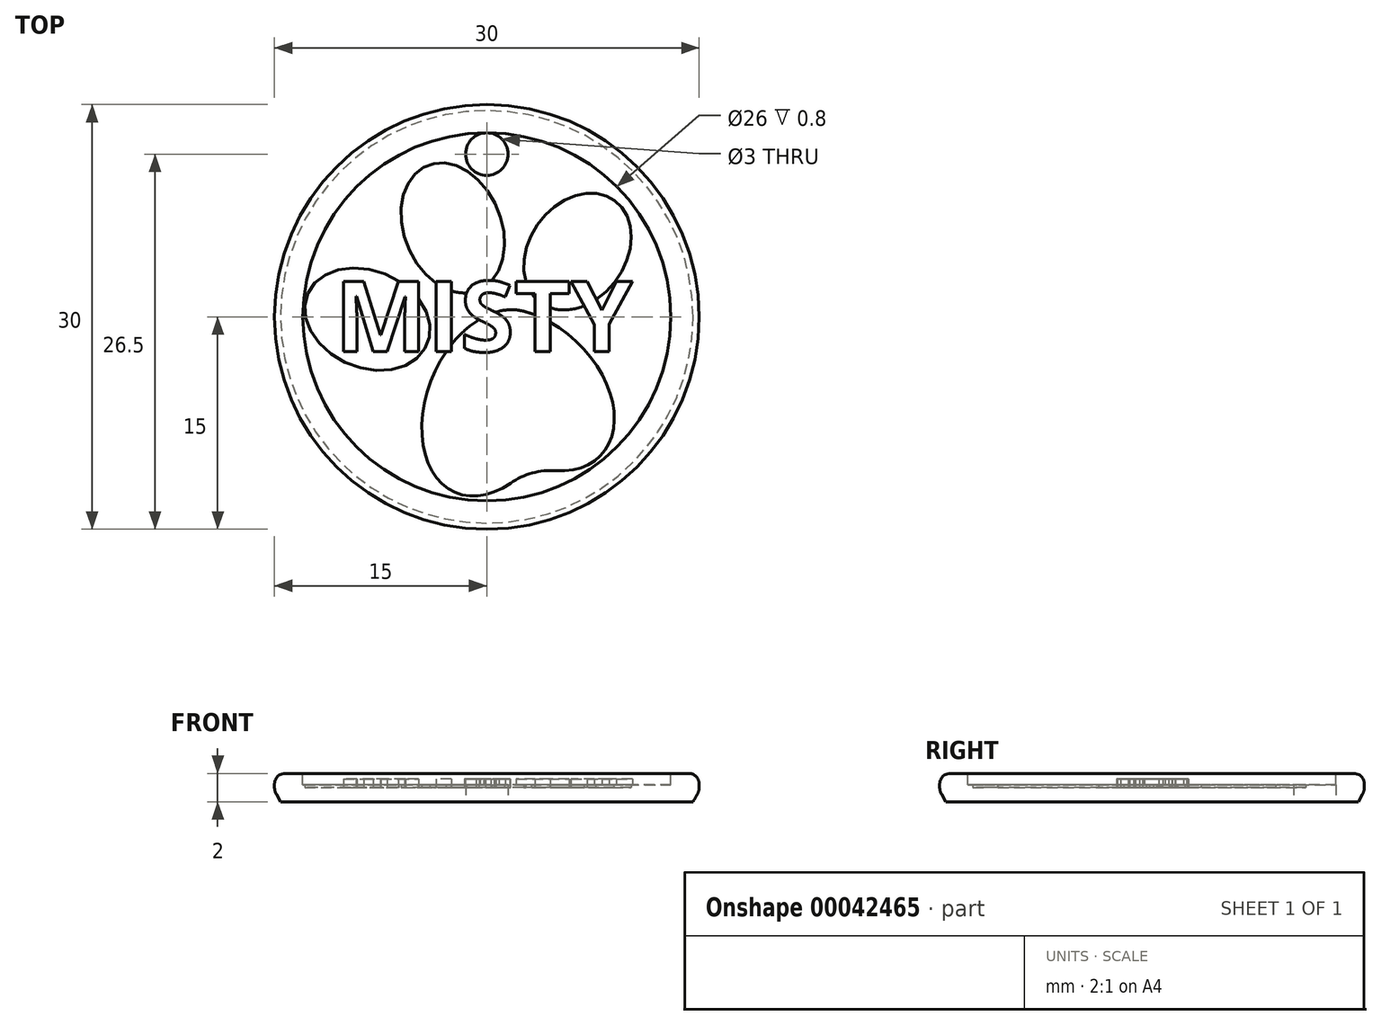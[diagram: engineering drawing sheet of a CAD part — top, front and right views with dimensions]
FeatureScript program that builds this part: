
annotation { "Feature Type Name" : "Feature", "Feature Type Description" : "" }
export const myFeature = defineFeature(function(context is Context, id is Id, definition is map)
    precondition{}
    {
        {
            var Q0;
            Q0=qCreatedBy(makeId("Top.planeOp"),FACE);
            var sketch = newSketch(context, id + "F0", { "sketchPlane" : qUnion([Q0])});
            skCircle(sketch, "E0", {"center": v(0, 0) * mm, "radius": 15 * mm});
            skSolve(sketch);
        }
        {
            var Q0;
            Q0 = qSketchRegion(id + "F0", true);
            extrude(context, id + "F1", {"entities" : qUnion([Q0]), "depth" : 2 * mm});
        }
        {
            var Q0;
            Q0=makeQuery(id+"F1.opExtrude","CAP_FACE",FACE,{"disambiguationData":[OSD([sQuery(id+"F0.wireOp",EDGE,"E0")])],"isStart":false});
            var sketch = newSketch(context, id + "F2", { "sketchPlane" : qUnion([Q0])});
            skCircle(sketch, "E1", {"center": v(0, 0) * mm, "radius": 13 * mm});
            skSolve(sketch);
        }
        {
            var Q0;
            Q0 = qSketchRegion(id + "F2", true);
            extrude(context, id + "F3", {"entities" : qUnion([Q0]), "operationType" : NewBodyOperationType.REMOVE, "oppositeDirection" : true, "depth" : 0.8 * mm});
        }
        {
            var Q0;
            Q0=makeQuery(id+"F3.boolean.opBoolean","COPY",FACE,{"derivedFrom":makeQuery(id+"F3.opExtrude","CAP_FACE",FACE,{"disambiguationData":[OSD([sQuery(id+"F2.wireOp",EDGE,"E1")])],"isStart":false})});
            var sketch = newSketch(context, id + "F4", { "sketchPlane" : qUnion([Q0])});
            skEllipse(sketch, "E2", {"center": v(-8.44, -0.16) * mm, "majorRadius": 4.58 * mm, "minorRadius": 3.42 * mm, "majorAxis": v(0.92, -0.39)});
            skEllipse(sketch, "E3", {"center": v(-2.4, 6.28) * mm, "majorRadius": 4.76 * mm, "minorRadius": 3.44 * mm, "majorAxis": v(0.38, -0.93)});
            skEllipse(sketch, "E4", {"center": v(6.4, 4.62) * mm, "majorRadius": 4.46 * mm, "minorRadius": 3.4 * mm, "majorAxis": v(0.58, 0.81)});
            skEllipticalArc(sketch, "E5", {});
            skEllipticalArc(sketch, "E6", {});
            skPoint(sketch, "E7.visualSharp", {"position": v(2.62, 0.4) * mm});
            skArc(sketch, "E7.filletArc", {"start": v(4.87, -10.86) * mm, "mid": v(3.2, -11.03) * mm, "end": v(1.68, -11.75) * mm});
            const initialGuessF4  = {"E5": [0.00039821620125618366, -0.006079853733279628, 0.3754317400528692, 0.9268500464265377, 0.006854673766816253, 0.004617638328241886, 0.08123967665926242, 3.942349918397179], "E6": [0.0031306940243142093, -0.005130720116552976, 0.7281276660444532, -0.6854415379452705, 0.006774684959826952, 0.004649626096762248, 5.58687193887531, 2.2321898580311177]};
            skSetInitialGuess(sketch, initialGuessF4);
            skSolve(sketch);
        }
        {
            var Q0;
            Q0 = qSketchRegion(id + "F4", true);
            extrude(context, id + "F5", {"entities" : qUnion([Q0]), "operationType" : NewBodyOperationType.REMOVE, "oppositeDirection" : true, "depth" : 0.2 * mm});
        }
        {
            var Q0;
            Q0=qCreatedBy(makeId("Top.planeOp"),FACE);
            var sketch = newSketch(context, id + "F6", { "sketchPlane" : qUnion([Q0])});
            skLineSegment(sketch, "E8", {"start": v(0, 0.05) * mm, "end": v(0, -0.05) * mm, "construction": true});
            skSolve(sketch);
        }
        {
            var Q0;
            Q0=makeQuery(id+"F3.boolean.opBoolean","COPY",FACE,{"derivedFrom":makeQuery(id+"F3.opExtrude","CAP_FACE",FACE,{"disambiguationData":[OSD([sQuery(id+"F2.wireOp",EDGE,"E1")])],"isStart":false})});
            var sketch = newSketch(context, id + "F7", { "sketchPlane" : qUnion([Q0])});
            skText(sketch, "E9", { "text": "MISTY", "fontName": "OpenSans-Bold.ttf"});
            const initialGuessF7  = {"E9": [-0.01074, -0.00245, 1, 0, 0.005]};
            skSetInitialGuess(sketch, initialGuessF7);
            skSolve(sketch);
        }
        {
            var Q0;
            Q0 = qSketchRegion(id + "F7", true);
            extrude(context, id + "F8", {"entities" : qUnion([Q0]), "operationType" : NewBodyOperationType.ADD, "depth" : 0.4 * mm, "hasSecondDirection" : true, "secondDirectionOppositeDirection" : true, "secondDirectionDepth" : 0.5 * mm});
        }
        {
            var Q0;
            Q0=qCreatedBy(makeId("Top.planeOp"),FACE);
            var sketch = newSketch(context, id + "F9", { "sketchPlane" : qUnion([Q0])});
            skCircle(sketch, "E10", {"center": v(0, 11.5) * mm, "radius": 1.5 * mm});
            skSolve(sketch);
        }
        {
            var Q0;
            Q0 = qSketchRegion(id + "F9", true);
            extrude(context, id + "F10", {"entities" : qUnion([Q0]), "operationType" : NewBodyOperationType.REMOVE, "endBound" : BoundingType.THROUGH_ALL, "depth" : 25 * mm});
        }
        {
            var Q0;
            Q0=makeQuery(id+"F8.opExtrude","CAP_EDGE",EDGE,{"disambiguationData":[OSD([sQuery(id+"F0.wireOp",EDGE,"E0")])],"isStart":false});
            var Q1;
            Q1=makeQuery(id+"F8.opExtrude","CAP_EDGE",EDGE,{"disambiguationData":[OSD([sQuery(id+"F2.wireOp",EDGE,"E1")])],"isStart":false});
            var Q2;
            Q2=makeQuery(id+"F1.opExtrude","CAP_EDGE",EDGE,{"disambiguationData":[OSD([sQuery(id+"F0.wireOp",EDGE,"E0")])],"isStart":false});
            var Q3;
            Q3=makeQuery(id+"F3.boolean.opBoolean","COPY",EDGE,{"derivedFrom":makeQuery(id+"F3.opExtrude","CAP_EDGE",EDGE,{"disambiguationData":[OSD([sQuery(id+"F2.wireOp",EDGE,"E1")])],"isStart":true})});
            fillet(context, id + "F11", {"entities" : qUnion([Q0, Q1, Q2, Q3]), "radius" : 0.75 * mm, "tangentPropagation" : true, "allowEdgeOverflow" : false});
        }
        {
            var Q0;
            Q0=makeQuery(id+"F1.opExtrude","CAP_EDGE",EDGE,{"disambiguationData":[OSD([sQuery(id+"F0.wireOp",EDGE,"E0")])],"isStart":true});
            chamfer(context, id + "F12", {"entities" : qUnion([Q0]), "chamferType" : ChamferType.OFFSET_ANGLE, "width" : 0.75 * mm, "oppositeDirection" : false, "angle" : 30 * degree, "tangentPropagation" : true});
        }
        {
            var Q0;
            {var subQ0=sQuery(id+"F0.wireOp",EDGE,"E0");Q0=makeQuery(id+"F12.opChamfer","BLEND_EDGE",EDGE,{"blendedFrom":[makeQuery(id+"F1.opExtrude","CAP_EDGE",EDGE,{"disambiguationData":[OSD([subQ0])],"isStart":true}),makeQuery(id+"F8.boolean.opBoolean","MERGE",FACE,{"derivedFrom":[makeQuery(id+"F1.opExtrude","SWEPT_FACE",FACE,{"disambiguationData":[OSD([subQ0])]}),makeQuery(id+"F8.opExtrude","SWEPT_FACE",FACE,{"disambiguationData":[OSD([subQ0])]})]})],"blendedInto":[makeQuery(id+"F8.boolean.opBoolean","MERGE",FACE,{"derivedFrom":[makeQuery(id+"F1.opExtrude","SWEPT_FACE",FACE,{"disambiguationData":[OSD([subQ0])]}),makeQuery(id+"F8.opExtrude","SWEPT_FACE",FACE,{"disambiguationData":[OSD([subQ0])]})]})]});}
            fillet(context, id + "F13", {"entities" : qUnion([Q0]), "radius" : 1 * mm, "tangentPropagation" : true, "allowEdgeOverflow" : false});
        }
    });
